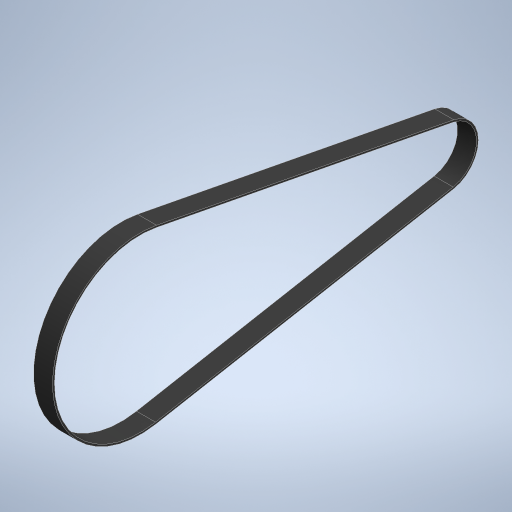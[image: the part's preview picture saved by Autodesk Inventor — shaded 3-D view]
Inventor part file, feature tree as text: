
AUTODESK INVENTOR PART (.ipt)
format: ipt  version: 2023 (Build 270158000, 158)  size: 251,904 bytes
history: native  units: mm
features: other x1, extrude x1, sketch x1
ambient origin geometry x8: Origin, YZ Plane, XZ Plane, XY Plane, X Axis, Y Axis, Z Axis, Center Point
bodies: Body1 (feature_tree)
feature tree (3):
  other  "ソリッド1"
  extrude  "押し出し1"  Depth=92.0mm
  sketch  "スケッチ1"
